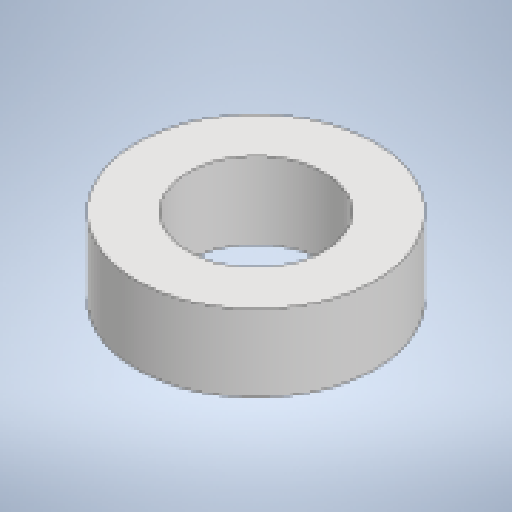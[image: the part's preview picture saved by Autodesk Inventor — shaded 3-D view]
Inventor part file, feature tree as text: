
AUTODESK INVENTOR PART (.ipt)
format: ipt  version: 2025.1 (Build 291241000, 241)  size: 128,000 bytes
history: native  units: mm
features: other x3, extrude x1, sketch x1, reference x1
ambient origin geometry x8: Origin, YZ Plane, XZ Plane, XY Plane, X Axis, Y Axis, Z Axis, Center Point
bodies: Solid1 (feature_tree)
feature tree (6):
  extrude  "Extrusion1"  Depth=4.5mm TaperAngle=0.0deg
  sketch  "Sketch1"  dims[d0=14.0mm d1=4.5mm d2=0.0mm]
  reference  "Reference1"
  parser-record x1  (decoder bookkeeping rows leaked as tree rows — omitted from the tree; the rows remain in map.json)
  other  "Welle.iam"
  other  "201 part 3:2"
note: 1 file-system path scrubbed to <path> (originals preserved in map.json)
